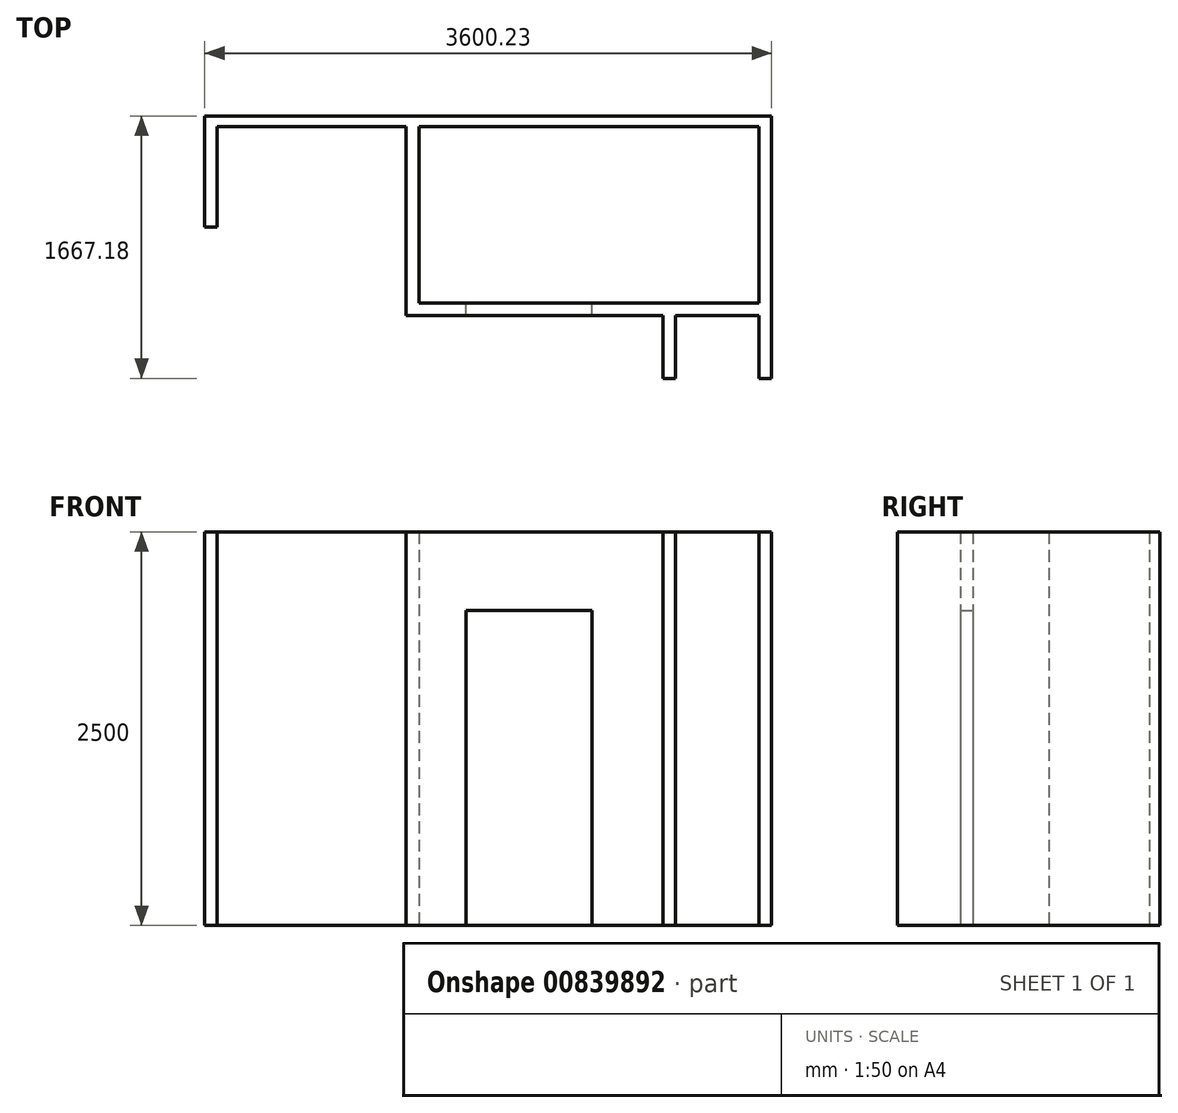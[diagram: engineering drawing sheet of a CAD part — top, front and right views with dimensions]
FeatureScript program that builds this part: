
annotation { "Feature Type Name" : "Feature", "Feature Type Description" : "" }
export const myFeature = defineFeature(function(context is Context, id is Id, definition is map)
    precondition{}
    {
        {
            var Q0;
            Q0=qCreatedBy(makeId("Top.planeOp"),FACE);
            var sketch = newSketch(context, id + "F0", { "sketchPlane" : qUnion([Q0])});
            skLineSegment(sketch, "E0", {"start": v(-892.9, 721.92) * mm, "end": v(-892.9, 1360.54) * mm});
            skLineSegment(sketch, "E1", {"start": v(-892.9, 721.92) * mm, "end": v(-972.9, 721.92) * mm});
            skLineSegment(sketch, "E2", {"start": v(-972.9, 721.92) * mm, "end": v(-972.9, 1427.7) * mm});
            skLineSegment(sketch, "E3", {"start": v(-972.9, 1427.7) * mm, "end": v(2627.1, 1427.7) * mm});
            skLineSegment(sketch, "E4", {"start": v(-892.9, 1360.54) * mm, "end": v(307.1, 1360.54) * mm});
            skLineSegment(sketch, "E5", {"start": v(307.1, 1360.54) * mm, "end": v(307.1, 160.54) * mm});
            skLineSegment(sketch, "E6", {"start": v(387.1, 1360.54) * mm, "end": v(2547.3, 1360.54) * mm});
            skLineSegment(sketch, "E7", {"start": v(2627.29, 160.54) * mm, "end": v(2627.1, 1427.7) * mm});
            skLineSegment(sketch, "E8", {"start": v(2547.3, 1360.54) * mm, "end": v(2547.47, 240.69) * mm});
            skLineSegment(sketch, "E9", {"start": v(387.1, 1360.54) * mm, "end": v(387.1, 240.54) * mm});
            skLineSegment(sketch, "E10", {"start": v(687.1, 160.54) * mm, "end": v(687.1, 240.54) * mm});
            skLineSegment(sketch, "E11", {"start": v(687.1, 240.54) * mm, "end": v(387.1, 240.54) * mm});
            skLineSegment(sketch, "E12", {"start": v(1487.1, 160.54) * mm, "end": v(1937.29, 160.54) * mm});
            skLineSegment(sketch, "E13", {"start": v(1487.1, 160.54) * mm, "end": v(1487.1, 240.54) * mm});
            skLineSegment(sketch, "E14", {"start": v(1487.1, 240.54) * mm, "end": v(2547.47, 240.69) * mm});
            skLineSegment(sketch, "E15", {"start": v(687.1, 160.54) * mm, "end": v(307.1, 160.54) * mm});
            skLineSegment(sketch, "E16", {"start": v(2627.29, 160.54) * mm, "end": v(2627.34, -239.46) * mm});
            skLineSegment(sketch, "E17", {"start": v(2627.34, -239.46) * mm, "end": v(2547.34, -239.48) * mm});
            skLineSegment(sketch, "E18", {"start": v(2547.34, -239.48) * mm, "end": v(2547.48, 160.54) * mm});
            skLineSegment(sketch, "E19", {"start": v(2017.34, -239.3) * mm, "end": v(2017.29, 160.54) * mm});
            skLineSegment(sketch, "E20", {"start": v(2017.34, -239.3) * mm, "end": v(1937.34, -239.3) * mm});
            skLineSegment(sketch, "E21", {"start": v(1937.34, -239.3) * mm, "end": v(1937.29, 160.54) * mm});
            skLineSegment(sketch, "E22.trimOffspring", {"start": v(2017.29, 160.54) * mm, "end": v(2547.48, 160.54) * mm});
            skSolve(sketch);
        }
        {
            var Q0;
            Q0=makeQuery(id+"F0.imprint","IMPRINT",FACE,{"disambiguationData":[TD([[makeQuery(id+"F0.imprint","IMPRINT",EDGE,{"derivedFrom":sQuery(id+"F0.wireOp",EDGE,"E0")}),1.0]])]});
            extrude(context, id + "F1", {"entities" : qUnion([Q0]), "depth" : 2500 * mm, "offsetDistance" : 25 * mm});
        }
        {
            var Q0;
            Q0=makeQuery(id+"F1.opExtrude","SWEPT_FACE",FACE,{"disambiguationData":[OSD([sQuery(id+"F0.wireOp",EDGE,"E10")])]});
            var sketch = newSketch(context, id + "F2", { "sketchPlane" : qUnion([Q0])});
            skLineSegment(sketch, "E23", {"start": v(160.54, 2500) * mm, "end": v(160.54, 2000) * mm});
            skLineSegment(sketch, "E24", {"start": v(160.54, 2000) * mm, "end": v(240.54, 2000) * mm});
            skSolve(sketch);
        }
        {
            var Q0;
            Q0=makeQuery(id+"F2.imprint","IMPRINT",FACE,{"disambiguationData":[TD([[makeQuery(id+"F2.imprint","IMPRINT",EDGE,{"derivedFrom":sQuery(id+"F2.wireOp",EDGE,"E23")}),1.0]])]});
            extrude(context, id + "F3", {"entities" : qUnion([Q0]), "operationType" : NewBodyOperationType.ADD, "depth" : 800 * mm, "offsetDistance" : 25 * mm});
        }
    });
